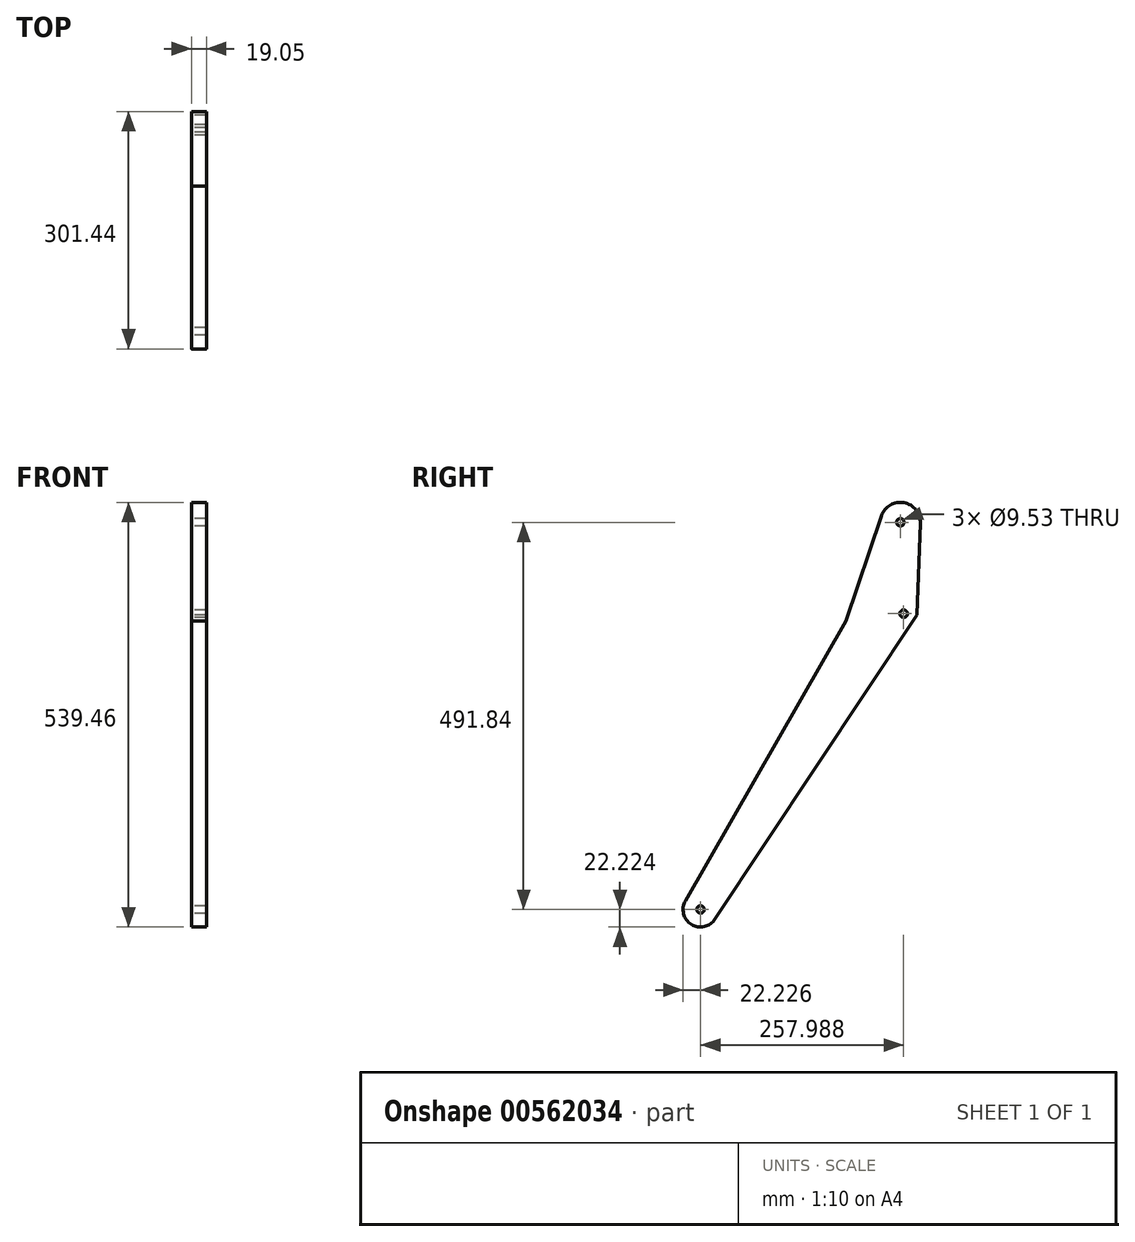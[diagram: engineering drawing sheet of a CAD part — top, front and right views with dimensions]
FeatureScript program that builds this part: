
annotation { "Feature Type Name" : "Feature", "Feature Type Description" : "" }
export const myFeature = defineFeature(function(context is Context, id is Id, definition is map)
    precondition{}
    {
        {
            var Q0;
            Q0=qCreatedBy(makeId("Right.planeOp"),FACE);
            var sketch = newSketch(context, id + "F0", { "sketchPlane" : qUnion([Q0])});
            skLineSegment(sketch, "E0", {"start": v(-513.86, 319.86) * mm, "end": v(-513.86, 78.56) * mm});
            skSolve(sketch);
        }
        {
            var Q0;
            Q0=qCreatedBy(makeId("Right.planeOp"),FACE);
            var sketch = newSketch(context, id + "F1", { "sketchPlane" : qUnion([Q0])});
            skLineSegment(sketch, "E1", {"start": v(-749.76, 256.37) * mm, "end": v(-601.81, 261.03) * mm});
            skLineSegment(sketch, "E2", {"start": v(-560.54, 653.66) * mm, "end": v(-601.81, 261.03) * mm});
            skLineSegment(sketch, "E3", {"start": v(-560.54, 653.66) * mm, "end": v(-749.76, 256.37) * mm});
            skLineSegment(sketch, "E4", {"start": v(-712.77, 291.22) * mm, "end": v(-723.7, 436.42) * mm});
            skLineSegment(sketch, "E5", {"start": v(-712.77, 291.22) * mm, "end": v(-826.16, 542.64) * mm});
            skLineSegment(sketch, "E6", {"start": v(-723.7, 436.42) * mm, "end": v(-826.16, 542.64) * mm});
            skLineSegment(sketch, "E7", {"start": v(-1007.93, 660.27) * mm, "end": v(-826.16, 542.64) * mm});
            skLineSegment(sketch, "E8", {"start": v(-1037.12, 677.37) * mm, "end": v(-1007.93, 660.27) * mm});
            skLineSegment(sketch, "E9", {"start": v(-1037.12, 677.37) * mm, "end": v(-712.77, 291.22) * mm});
            skLineSegment(sketch, "E10", {"start": v(-1007.93, 660.27) * mm, "end": v(-712.77, 291.22) * mm});
            skLineSegment(sketch, "E11", {"start": v(-601.81, 261.03) * mm, "end": v(-595.01, 401.75) * mm});
            skLineSegment(sketch, "E12", {"start": v(-601.81, 261.03) * mm, "end": v(-607.25, 655.88) * mm});
            skLineSegment(sketch, "E13", {"start": v(-595.01, 401.75) * mm, "end": v(-607.25, 655.88) * mm});
            skLineSegment(sketch, "E14", {"start": v(-723.7, 436.42) * mm, "end": v(-595.01, 401.75) * mm});
            skLineSegment(sketch, "E15", {"start": v(-826.16, 542.64) * mm, "end": v(-774.61, 590.25) * mm});
            skLineSegment(sketch, "E16", {"start": v(-749.76, 256.37) * mm, "end": v(-774.61, 590.25) * mm});
            skLineSegment(sketch, "E17", {"start": v(-1041.29, 793.41) * mm, "end": v(-774.61, 590.25) * mm});
            skLineSegment(sketch, "E18", {"start": v(-1390.78, 317.95) * mm, "end": v(-1336.8, 360.93) * mm});
            skLineSegment(sketch, "E19", {"start": v(-1336.8, 360.93) * mm, "end": v(-1295.1, 301.57) * mm});
            skLineSegment(sketch, "E20", {"start": v(-1041.29, 793.41) * mm, "end": v(-1295.1, 301.57) * mm});
            skLineSegment(sketch, "E21", {"start": v(-1295.1, 301.57) * mm, "end": v(-1037.12, 677.37) * mm});
            skLineSegment(sketch, "E22", {"start": v(-1037.12, 677.37) * mm, "end": v(-1041.29, 793.41) * mm});
            skLineSegment(sketch, "E23", {"start": v(-1007.93, 660.27) * mm, "end": v(-1336.8, 360.93) * mm});
            skLineSegment(sketch, "E24", {"start": v(-1390.78, 317.95) * mm, "end": v(-1295.1, 301.57) * mm});
            skLineSegment(sketch, "E25", {"start": v(-1295.1, 301.57) * mm, "end": v(-1295.1, 192.57) * mm});
            skLineSegment(sketch, "E26", {"start": v(-1295.1, 192.57) * mm, "end": v(-1403.22, 211.07) * mm});
            skLineSegment(sketch, "E27", {"start": v(-1403.22, 211.07) * mm, "end": v(-1390.78, 317.95) * mm});
            skLineSegment(sketch, "E28", {"start": v(-1390.78, 317.95) * mm, "end": v(-1295.1, 192.57) * mm});
            skLineSegment(sketch, "E29", {"start": v(0, 0) * mm, "end": v(0, 674.17) * mm});
            skLineSegment(sketch, "E30", {"start": v(-316.61, 320.6) * mm, "end": v(-316.61, 307.94) * mm});
            skLineSegment(sketch, "E31", {"start": v(-400.45, 218.07) * mm, "end": v(-378.01, 218.07) * mm});
            skLineSegment(sketch, "E32", {"start": v(-472.6, 74.76) * mm, "end": v(-472.6, 54.94) * mm});
            skSolve(sketch);
        }
        {
            var Q0;
            Q0=qCreatedBy(makeId("Right.planeOp"),FACE);
            var sketch = newSketch(context, id + "F2", { "sketchPlane" : qUnion([Q0])});
            skArc(sketch, "E33", {"start": v(-1065.36, 801.53) * mm, "mid": v(-1036.69, 818.4) * mm, "end": v(-1015.9, 792.42) * mm});
            skArc(sketch, "E34", {"start": v(-1276.58, 289.3) * mm, "mid": v(-1306.78, 282.66) * mm, "end": v(-1314.38, 312.64) * mm});
            skLineSegment(sketch, "E35", {"start": v(-1314.38, 312.64) * mm, "end": v(-1110.36, 668) * mm});
            skLineSegment(sketch, "E36", {"start": v(-1110.36, 668) * mm, "end": v(-1065.36, 801.53) * mm});
            skLineSegment(sketch, "E37", {"start": v(-1015.9, 792.42) * mm, "end": v(-1020.5, 675.81) * mm});
            skLineSegment(sketch, "E38", {"start": v(-1020.5, 675.81) * mm, "end": v(-1276.58, 289.3) * mm});
            skCircle(sketch, "E39", {"center": v(-1041.29, 793.41) * mm, "radius": 4.76 * mm});
            skCircle(sketch, "E40", {"center": v(-1037.12, 677.37) * mm, "radius": 4.76 * mm});
            skCircle(sketch, "E41", {"center": v(-1295.1, 301.57) * mm, "radius": 4.76 * mm});
            skSolve(sketch);
        }
        {
            var Q0;
            Q0=qSketchRegion(id+"F2",true);
            extrude(context, id + "F3", {"entities" : qUnion([Q0]), "depth" : 19.05 * mm, "offsetDistance" : 25.4 * mm});
        }
    });
